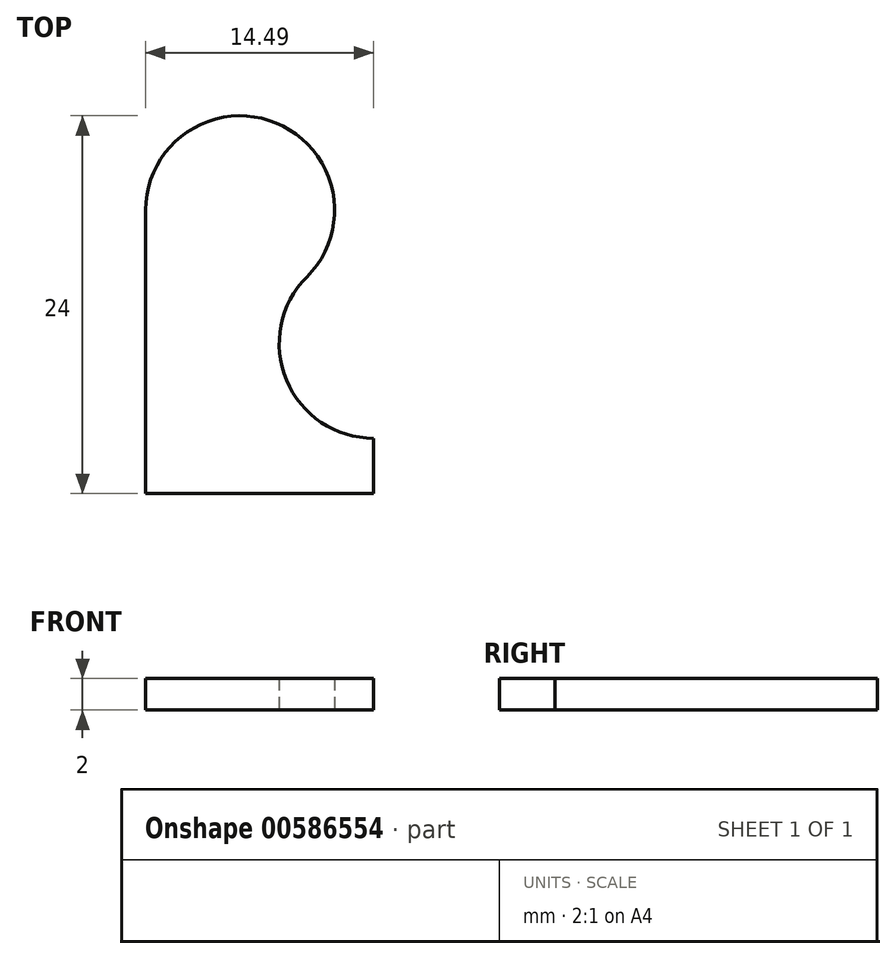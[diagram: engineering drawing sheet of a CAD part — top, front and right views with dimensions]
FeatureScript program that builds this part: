
annotation { "Feature Type Name" : "Feature", "Feature Type Description" : "" }
export const myFeature = defineFeature(function(context is Context, id is Id, definition is map)
    precondition{}
    {
        {
            var Q0;
            Q0=qCreatedBy(makeId("Top.planeOp"),FACE);
            var sketch = newSketch(context, id + "F0", { "sketchPlane" : qUnion([Q0])});
            skLineSegment(sketch, "E0", {"start": v(0, 0) * mm, "end": v(0, 18) * mm});
            skArc(sketch, "E1", {"start": v(0, 18) * mm, "mid": v(8.3, 23.54) * mm, "end": v(10.24, 13.76) * mm});
            skArc(sketch, "E2", {"start": v(10.24, 13.76) * mm, "mid": v(8.94, 7.22) * mm, "end": v(14.49, 3.51) * mm});
            skLineSegment(sketch, "E3", {"start": v(6, 18) * mm, "end": v(14.49, 9.51) * mm, "construction": true});
            skLineSegment(sketch, "E4", {"start": v(14.49, 0) * mm, "end": v(14.49, 9.51) * mm, "construction": true});
            skLineSegment(sketch, "E5", {"start": v(0, 0) * mm, "end": v(14.49, 0) * mm});
            skLineSegment(sketch, "E6", {"start": v(14.49, 3.51) * mm, "end": v(14.49, 0) * mm});
            skLineSegment(sketch, "E7", {"start": v(0, 18) * mm, "end": v(6, 18) * mm, "construction": true});
            skLineSegment(sketch, "E8", {"start": v(6, 18) * mm, "end": v(6, 12) * mm, "construction": true});
            skLineSegment(sketch, "E9", {"start": v(6, 12) * mm, "end": v(6, 6) * mm, "construction": true});
            skLineSegment(sketch, "E10", {"start": v(6, 0) * mm, "end": v(6, 6) * mm, "construction": true});
            skSolve(sketch);
        }
        {
            var Q0;
            Q0=qSketchRegion(id+"F0",true);
            extrude(context, id + "F1", {"entities" : qUnion([Q0]), "depth" : 2 * mm, "offsetDistance" : 25 * mm});
        }
    });
